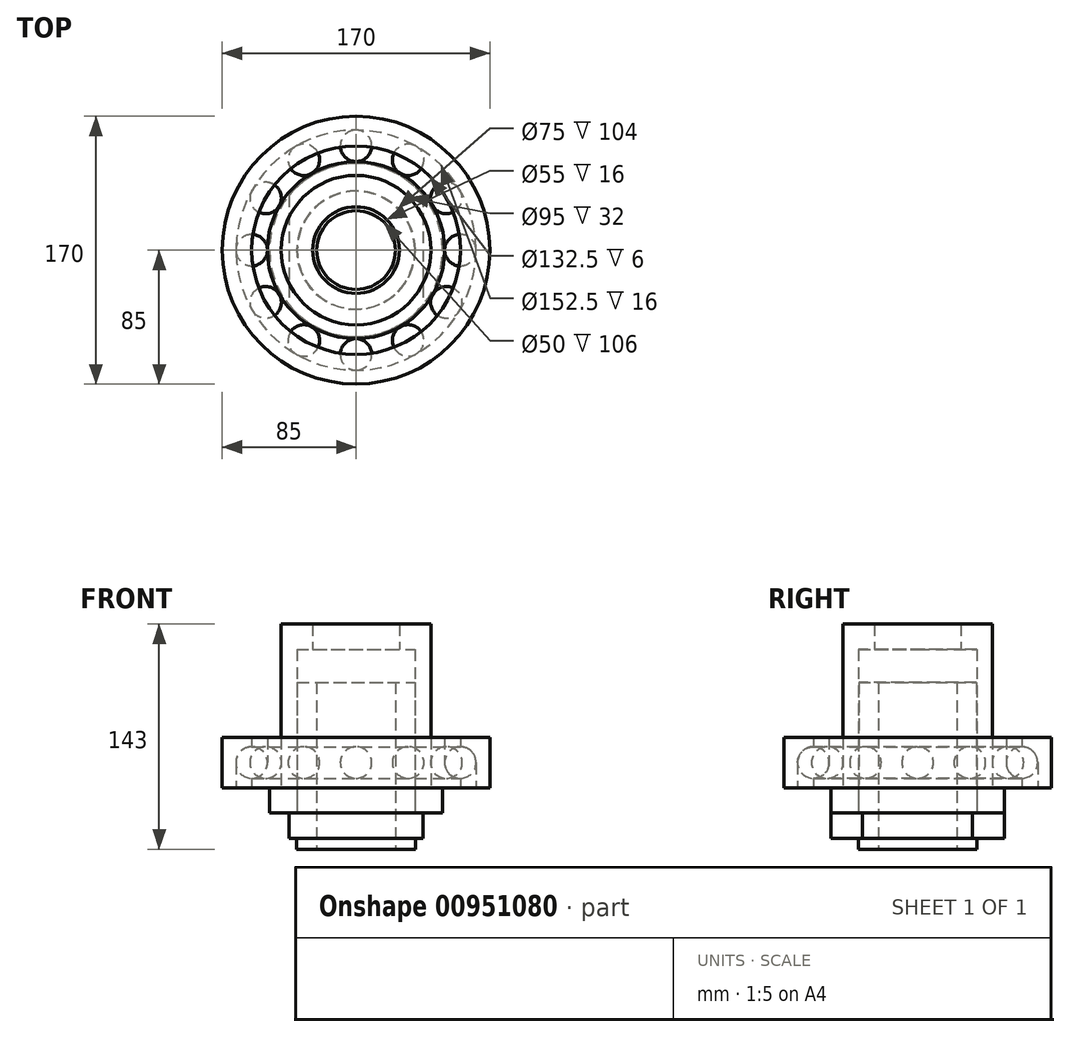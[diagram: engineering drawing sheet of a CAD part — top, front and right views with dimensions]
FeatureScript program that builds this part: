
annotation { "Feature Type Name" : "Feature", "Feature Type Description" : "" }
export const myFeature = defineFeature(function(context is Context, id is Id, definition is map)
    precondition{}
    {
        {
            var Q0;
            Q0=qCreatedBy(makeId("Front.planeOp"),FACE);
            var sketch = newSketch(context, id + "F0", { "sketchPlane" : qUnion([Q0])});
            skLineSegment(sketch, "E0", {"start": v(0, -7) * mm, "end": v(0, 99) * mm});
            skLineSegment(sketch, "E1", {"start": v(0, 99) * mm, "end": v(37.38, 99) * mm});
            skLineSegment(sketch, "E2", {"start": v(37.37, 99) * mm, "end": v(37.38, 32) * mm});
            skLineSegment(sketch, "E3", {"start": v(37.38, 32) * mm, "end": v(37.5, 32) * mm});
            skLineSegment(sketch, "E4", {"start": v(37.5, 32) * mm, "end": v(37.5, 16) * mm});
            skLineSegment(sketch, "E5", {"start": v(37.5, 16) * mm, "end": v(55, 16) * mm});
            skLineSegment(sketch, "E6", {"start": v(55, 16) * mm, "end": v(55, 0) * mm});
            skLineSegment(sketch, "E7", {"start": v(55, 0) * mm, "end": v(37.65, 0) * mm});
            skLineSegment(sketch, "E8", {"start": v(37.65, 0) * mm, "end": v(37.65, -7) * mm});
            skLineSegment(sketch, "E9", {"start": v(37.65, -7) * mm, "end": v(0, -7) * mm});
            skLineSegment(sketch, "E10.MirrorCS", {"start": v(-37.37, 99) * mm, "end": v(-37.38, 32) * mm, "construction": true});
            skLineSegment(sketch, "E11.MirrorCS", {"start": v(-37.5, 32) * mm, "end": v(-37.5, 16) * mm, "construction": true});
            skLineSegment(sketch, "E12.MirrorCS", {"start": v(-55, 16) * mm, "end": v(-55, 0) * mm, "construction": true});
            skLineSegment(sketch, "E13.MirrorCS", {"start": v(-37.65, 0) * mm, "end": v(-37.65, -7) * mm, "construction": true});
            skLineSegment(sketch, "E14", {"start": v(25, 99) * mm, "end": v(25, -7) * mm});
            skLineSegment(sketch, "E15.MirrorCS", {"start": v(-25, 99) * mm, "end": v(-25, -7) * mm, "construction": true});
            skLineSegment(sketch, "E16", {"start": v(55, 16) * mm, "end": v(55, 32) * mm});
            skLineSegment(sketch, "E17", {"start": v(55, 32) * mm, "end": v(47.5, 32) * mm});
            skLineSegment(sketch, "E18", {"start": v(47.5, 32) * mm, "end": v(47.5, 136) * mm});
            skLineSegment(sketch, "E19", {"start": v(47.5, 136) * mm, "end": v(37.5, 136) * mm});
            skLineSegment(sketch, "E20", {"start": v(37.5, 136) * mm, "end": v(37.5, 32) * mm});
            skLineSegment(sketch, "E21.bottom", {"start": v(37.5, 136) * mm, "end": v(27.5, 136) * mm});
            skLineSegment(sketch, "E21.top", {"start": v(37.5, 120) * mm, "end": v(27.5, 120) * mm});
            skLineSegment(sketch, "E21.left", {"start": v(37.5, 136) * mm, "end": v(37.5, 120) * mm});
            skLineSegment(sketch, "E21.right", {"start": v(27.5, 136) * mm, "end": v(27.5, 120) * mm});
            skLineSegment(sketch, "E22.MirrorCS", {"start": v(-47.5, 32) * mm, "end": v(-47.5, 136) * mm, "construction": true});
            skLineSegment(sketch, "E23", {"start": v(47.5, 64) * mm, "end": v(85, 64) * mm});
            skLineSegment(sketch, "E24", {"start": v(85, 64) * mm, "end": v(85, 32) * mm});
            skLineSegment(sketch, "E25", {"start": v(85, 32) * mm, "end": v(55, 32) * mm});
            skLineSegment(sketch, "E26.MirrorCS", {"start": v(-85, 64) * mm, "end": v(-85, 32) * mm, "construction": true});
            skCircle(sketch, "E27", {"center": v(66.25, 48) * mm, "radius": 10 * mm});
            skPoint(sketch, "E27.centerSnap0", {"position": v(85, 48) * mm});
            skPoint(sketch, "E27.centerSnap1", {"position": v(66.25, 64) * mm});
            skLineSegment(sketch, "E28", {"start": v(66.25, 64) * mm, "end": v(66.25, 58) * mm});
            skLineSegment(sketch, "E29", {"start": v(66.25, 58) * mm, "end": v(66.25, 38) * mm});
            skLineSegment(sketch, "E30", {"start": v(66.25, 38) * mm, "end": v(66.25, 32) * mm});
            skLineSegment(sketch, "E31", {"start": v(56.25, 48) * mm, "end": v(56.25, 64) * mm});
            skLineSegment(sketch, "E32", {"start": v(76.25, 48) * mm, "end": v(76.25, 32) * mm});
            skSolve(sketch);
        }
        {
            var Q0;
            {var subQ0=sQuery(id+"F0.wireOp",EDGE,"E2");Q0=makeQuery(id+"F0.imprint","IMPRINT",FACE,{"disambiguationData":[TD([[makeQuery(id+"F0.imprint","IMPRINT",EDGE,{"derivedFrom":subQ0}),-1.0]])]});}
            var Q1;
            Q1=sQuery(id+"F0.wireOp",EDGE,"E0");
            revolve(context, id + "F1", {"surfaceOperationType" : NewSurfaceOperationType.NEW, "entities" : qUnion([Q0]), "axis" : qUnion([Q1]), "revolveType" : RevolveType.FULL});
        }
        {
            var Q0;
            Q0=qCreatedBy(makeId("Top.planeOp"),FACE);
            var sketch = newSketch(context, id + "F2", { "sketchPlane" : qUnion([Q0])});
            skLineSegment(sketch, "E33.bottom", {"start": v(-42.5, -55) * mm, "end": v(42.5, -55) * mm});
            skLineSegment(sketch, "E33.top", {"start": v(-42.5, 55) * mm, "end": v(42.5, 55) * mm});
            skLineSegment(sketch, "E33.left", {"start": v(-42.5, -55) * mm, "end": v(-42.5, 55) * mm});
            skLineSegment(sketch, "E33.right", {"start": v(42.5, -55) * mm, "end": v(42.5, 55) * mm});
            skPoint(sketch, "E33.middle", {"position": v(0, 0) * mm});
            skSolve(sketch);
        }
        {
            var Q0;
            Q0=makeQuery(id+"F2.imprint","IMPRINT",FACE,{"disambiguationData":[TD([[makeQuery(id+"F2.imprint","IMPRINT",EDGE,{"derivedFrom":sQuery(id+"F2.wireOp",EDGE,"E33.bottom")}),1.0]])]});
            extrude(context, id + "F3", {"entities" : qUnion([Q0]), "operationType" : NewBodyOperationType.INTERSECT, "endBound" : BoundingType.THROUGH_ALL, "depth" : 25 * mm, "offsetDistance" : 25 * mm, "hasSecondDirection" : true, "secondDirectionBound" : SecondDirectionBoundingType.THROUGH_ALL, "secondDirectionOppositeDirection" : true, "secondDirectionDepth" : 25 * mm});
        }
        {
            var Q0;
            Q0=makeQuery(id+"F0.imprint","IMPRINT",FACE,{"disambiguationData":[TD([[makeQuery(id+"F0.imprint","IMPRINT",EDGE,{"derivedFrom":sQuery(id+"F0.wireOp",EDGE,"E21.bottom")}),1.0]])]});
            var Q1;
            Q1=makeQuery(id+"F0.imprint","IMPRINT",FACE,{"disambiguationData":[TD([[makeQuery(id+"F0.imprint","IMPRINT",EDGE,{"derivedFrom":sQuery(id+"F0.wireOp",EDGE,"E4")}),1.0]])]});
            var Q2;
            Q2=sQuery(id+"F0.wireOp",EDGE,"E0");
            revolve(context, id + "F4", {"surfaceOperationType" : NewSurfaceOperationType.NEW, "entities" : qUnion([Q0, Q1]), "axis" : qUnion([Q2]), "revolveType" : RevolveType.FULL});
        }
        {
            var Q0;
            {var subQ4=sQuery(id+"F0.wireOp",EDGE,"E17");Q0=makeQuery(id+"F0.imprint","IMPRINT",FACE,{"disambiguationData":[TD([[makeQuery(id+"F0.imprint","IMPRINT",EDGE,{"derivedFrom":subQ4}),-1.0]])]});}
            var Q1;
            {var subQ1=sQuery(id+"F0.wireOp",EDGE,"E24");Q1=makeQuery(id+"F0.imprint","IMPRINT",FACE,{"disambiguationData":[TD([[makeQuery(id+"F0.imprint","IMPRINT",EDGE,{"derivedFrom":subQ1}),-1.0]])]});}
            var Q2;
            Q2=sQuery(id+"F0.wireOp",EDGE,"E0");
            revolve(context, id + "F5", {"surfaceOperationType" : NewSurfaceOperationType.NEW, "entities" : qUnion([Q0, Q1]), "axis" : qUnion([Q2]), "revolveType" : RevolveType.FULL});
        }
        {
            var Q0;
            {var subQ0=sQuery(id+"F0.wireOp",EDGE,"E29");Q0=makeQuery(id+"F0.imprint","IMPRINT",FACE,{"disambiguationData":[TD([[makeQuery(id+"F0.imprint","IMPRINT",EDGE,{"derivedFrom":subQ0}),-1.0]])]});}
            var Q1;
            Q1=sQuery(id+"F0.wireOp",EDGE,"E29");
            revolve(context, id + "F6", {"surfaceOperationType" : NewSurfaceOperationType.NEW, "entities" : qUnion([Q0]), "axis" : qUnion([Q1]), "revolveType" : RevolveType.FULL});
        }
        {
            var Q0;
            Q0=makeQuery(id+"F6.opRevolve","SWEPT_BODY",BODY,{"disambiguationData":[OSD([sQuery(id+"F0.wireOp",EDGE,"E27"),sQuery(id+"F0.wireOp",EDGE,"E29")])]});
            var Q1;
            Q1=sQuery(id+"F0.wireOp",EDGE,"E0");
            circularPattern(context, id + "F7", {"entities" : qUnion([Q0]), "axis" : qUnion([Q1]), "angle" : 360 * degree, "instanceCount" : 12, "equalSpace" : true});
        }
    });
